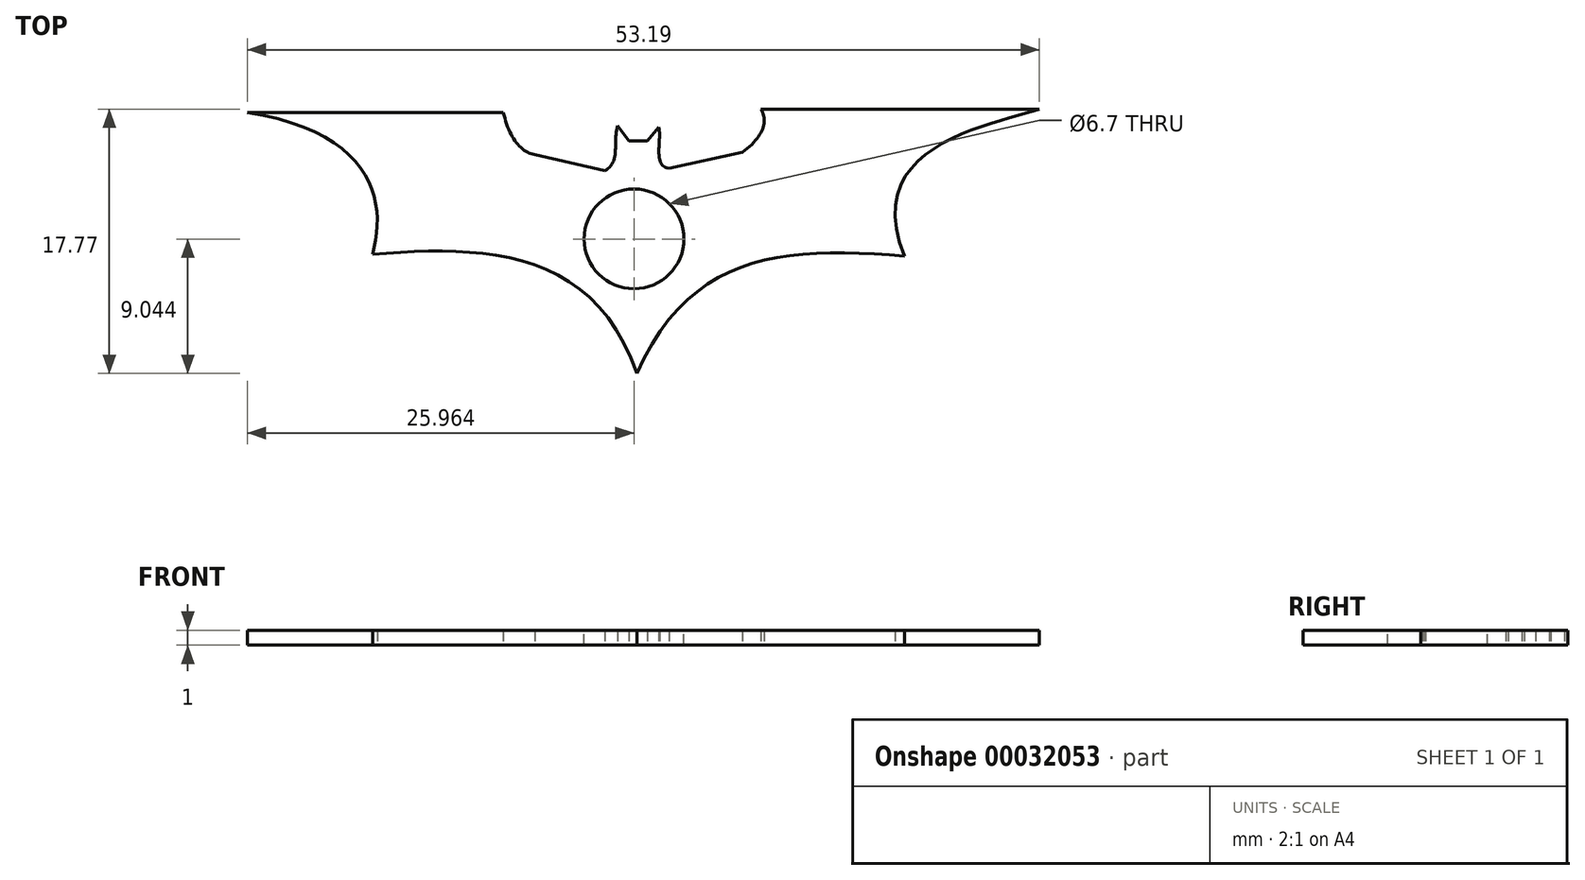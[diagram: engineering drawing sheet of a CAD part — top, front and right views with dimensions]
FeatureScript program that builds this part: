
annotation { "Feature Type Name" : "Feature", "Feature Type Description" : "" }
export const myFeature = defineFeature(function(context is Context, id is Id, definition is map)
    precondition{}
    {
        {
            var Q0;
            Q0=qCreatedBy(makeId("Top.planeOp"),FACE);
            var sketch = newSketch(context, id + "F0", { "sketchPlane" : qUnion([Q0])});
            skSolve(sketch);
        }
        {
            var Q0;
            Q0=qCreatedBy(makeId("Top.planeOp"),FACE);
            var sketch = newSketch(context, id + "F1", { "sketchPlane" : qUnion([Q0])});
            skLineSegment(sketch, "E0", {"start": v(9.1, -10.21) * mm, "end": v(13.8, -11.3) * mm});
            skLineSegment(sketch, "E1", {"start": v(14.65, -8.29) * mm, "end": v(15.42, -9.29) * mm});
            skLineSegment(sketch, "E2", {"start": v(16.65, -9.29) * mm, "end": v(17.42, -8.36) * mm});
            skLineSegment(sketch, "E3", {"start": v(18.11, -11.14) * mm, "end": v(23.04, -10.06) * mm});
            skLineSegment(sketch, "E4", {"start": v(24.28, -7.15) * mm, "end": v(42.99, -7.15) * mm});
            skLineSegment(sketch, "E5", {"start": v(-10.2, -7.37) * mm, "end": v(7, -7.37) * mm});
            skFitSpline(sketch, "E6", {"points": [v(-10.2, -7.37) * mm, v(-1.8, -16.9) * mm], "startDerivative": vector(25.54, -4.14) * mm, "endDerivative": vector(-2.88, -10.5) * mm});
            skFitSpline(sketch, "E7", {"points": [v(-1.8, -16.9) * mm, v(15.95, -24.92) * mm], "startDerivative": vector(21.39, 1.7) * mm, "endDerivative": vector(8.77, -25.73) * mm});
            skFitSpline(sketch, "E8", {"points": [v(15.95, -24.92) * mm, v(33.94, -17.03) * mm], "startDerivative": vector(11.08, 24.7) * mm, "endDerivative": vector(24.12, -1.92) * mm});
            skFitSpline(sketch, "E9", {"points": [v(33.94, -17.03) * mm, v(42.99, -7.15) * mm], "startDerivative": vector(-9.52, 22.8) * mm, "endDerivative": vector(8.74, 3.07) * mm});
            skFitSpline(sketch, "E10", {"points": [v(24.28, -7.15) * mm, v(23.04, -10.06) * mm], "startDerivative": vector(1.58, -2.55) * mm, "endDerivative": vector(-4.05, -3.04) * mm});
            skFitSpline(sketch, "E11", {"points": [v(18.11, -11.14) * mm, v(17.42, -8.36) * mm], "startDerivative": vector(-3.37, 0.48) * mm, "endDerivative": vector(-0.7, 2.77) * mm});
            skFitSpline(sketch, "E12", {"points": [v(14.65, -8.29) * mm, v(13.8, -11.3) * mm], "startDerivative": vector(-0.85, -3) * mm, "endDerivative": vector(-3.14, -1.44) * mm});
            skFitSpline(sketch, "E13", {"points": [v(9.1, -10.21) * mm, v(7, -7.37) * mm], "startDerivative": vector(-2.88, 0.41) * mm, "endDerivative": vector(-1, 4.8) * mm});
            skLineSegment(sketch, "E14", {"start": v(15.42, -9.29) * mm, "end": v(16.65, -9.29) * mm});
            skSolve(sketch);
        }
        {
            var Q0;
            Q0 = qSketchRegion(id + "F1", true);
            var Q1;
            Q1 = qSketchRegion(id + "F0", true);
            extrude(context, id + "F2", {"entities" : qUnion([Q0, Q1]), "depth" : 1 * mm});
        }
        {
            var Q0;
            Q0=makeQuery(id+"F2.opExtrude","CAP_FACE",FACE,{"disambiguationData":[OSD([sQuery(id+"F1.wireOp",EDGE,"E0"),sQuery(id+"F1.wireOp",EDGE,"E1"),sQuery(id+"F1.wireOp",EDGE,"E2"),sQuery(id+"F1.wireOp",EDGE,"E3"),sQuery(id+"F1.wireOp",EDGE,"E4"),sQuery(id+"F1.wireOp",EDGE,"E5"),sQuery(id+"F1.wireOp",EDGE,"E6"),sQuery(id+"F1.wireOp",EDGE,"E7"),sQuery(id+"F1.wireOp",EDGE,"E8"),sQuery(id+"F1.wireOp",EDGE,"E9"),sQuery(id+"F1.wireOp",EDGE,"E10"),sQuery(id+"F1.wireOp",EDGE,"E11"),sQuery(id+"F1.wireOp",EDGE,"E12"),sQuery(id+"F1.wireOp",EDGE,"E13"),sQuery(id+"F1.wireOp",EDGE,"E14")])],"isStart":false});
            shell(context, id + "F3", {"entities" : qUnion([Q0]), "thickness" : 1 * mm});
        }
        {
            var Q0;
            Q0=makeQuery(id+"F2.opExtrude","CAP_FACE",FACE,{"disambiguationData":[OSD([sQuery(id+"F1.wireOp",EDGE,"E0"),sQuery(id+"F1.wireOp",EDGE,"E1"),sQuery(id+"F1.wireOp",EDGE,"E2"),sQuery(id+"F1.wireOp",EDGE,"E3"),sQuery(id+"F1.wireOp",EDGE,"E4"),sQuery(id+"F1.wireOp",EDGE,"E5"),sQuery(id+"F1.wireOp",EDGE,"E6"),sQuery(id+"F1.wireOp",EDGE,"E7"),sQuery(id+"F1.wireOp",EDGE,"E8"),sQuery(id+"F1.wireOp",EDGE,"E9"),sQuery(id+"F1.wireOp",EDGE,"E10"),sQuery(id+"F1.wireOp",EDGE,"E11"),sQuery(id+"F1.wireOp",EDGE,"E12"),sQuery(id+"F1.wireOp",EDGE,"E13"),sQuery(id+"F1.wireOp",EDGE,"E14")])],"isStart":false});
            var sketch = newSketch(context, id + "F4", { "sketchPlane" : qUnion([Q0])});
            skCircle(sketch, "E15", {"center": v(15.76, -15.88) * mm, "radius": 3.35 * mm});
            skSolve(sketch);
        }
        {
            var Q0;
            Q0 = qSketchRegion(id + "F4", true);
            extrude(context, id + "F5", {"entities" : qUnion([Q0]), "operationType" : NewBodyOperationType.REMOVE, "oppositeDirection" : true, "depth" : 25.4 * mm});
        }
    });
